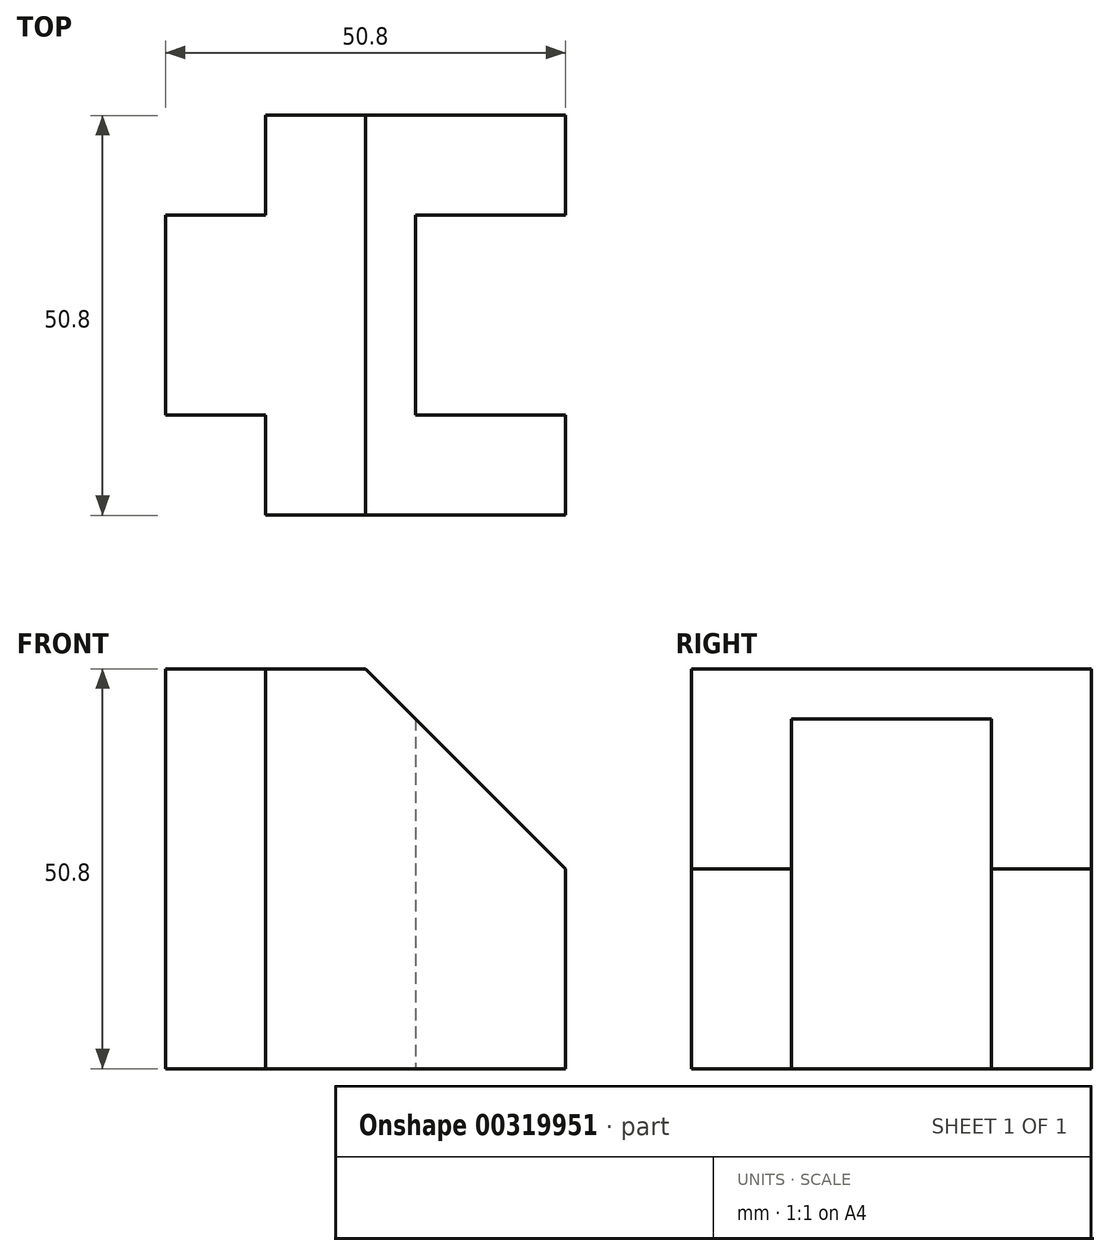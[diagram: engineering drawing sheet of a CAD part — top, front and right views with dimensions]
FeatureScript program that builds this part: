
annotation { "Feature Type Name" : "Feature", "Feature Type Description" : "" }
export const myFeature = defineFeature(function(context is Context, id is Id, definition is map)
    precondition{}
    {
        {
            var Q0;
            Q0=qCreatedBy(makeId("Top.planeOp"),FACE);
            var sketch = newSketch(context, id + "F0", { "sketchPlane" : qUnion([Q0])});
            skLineSegment(sketch, "E0", {"start": v(-18.83, 12.92) * mm, "end": v(6.57, 12.92) * mm});
            skLineSegment(sketch, "E1", {"start": v(6.57, 12.92) * mm, "end": v(19.27, 12.92) * mm});
            skLineSegment(sketch, "E2", {"start": v(19.27, 12.92) * mm, "end": v(19.27, 0.22) * mm});
            skLineSegment(sketch, "E3", {"start": v(19.27, 0.22) * mm, "end": v(0.22, 0.22) * mm});
            skLineSegment(sketch, "E4", {"start": v(0.22, 0.22) * mm, "end": v(0.22, -25.18) * mm});
            skLineSegment(sketch, "E5", {"start": v(0.22, -25.18) * mm, "end": v(19.27, -25.18) * mm});
            skLineSegment(sketch, "E6", {"start": v(19.27, -25.18) * mm, "end": v(19.27, -37.88) * mm});
            skLineSegment(sketch, "E7", {"start": v(19.27, -37.88) * mm, "end": v(6.57, -37.88) * mm});
            skLineSegment(sketch, "E8", {"start": v(6.57, -37.88) * mm, "end": v(-18.83, -37.88) * mm});
            skLineSegment(sketch, "E9", {"start": v(-18.83, -37.88) * mm, "end": v(-18.83, -25.18) * mm});
            skLineSegment(sketch, "E10", {"start": v(-18.83, -25.18) * mm, "end": v(-31.53, -25.18) * mm});
            skLineSegment(sketch, "E11", {"start": v(-31.53, -25.18) * mm, "end": v(-31.53, 0.22) * mm});
            skLineSegment(sketch, "E12", {"start": v(-31.53, 0.22) * mm, "end": v(-18.83, 0.22) * mm});
            skLineSegment(sketch, "E13", {"start": v(-18.83, 12.92) * mm, "end": v(-18.83, 0.22) * mm});
            skLineSegment(sketch, "E14", {"start": v(-6.13, 12.92) * mm, "end": v(-6.13, -37.88) * mm});
            skSolve(sketch);
        }
        {
            var Q0;
            Q0 = qSketchRegion(id + "F0", true);
            extrude(context, id + "F1", {"entities" : qUnion([Q0]), "depth" : 50.8 * mm});
        }
        {
            var Q0;
            Q0=makeQuery(id+"F1.opExtrude","SWEPT_FACE",FACE,{"disambiguationData":[OSD([sQuery(id+"F0.wireOp",EDGE,"E7"),sQuery(id+"F0.wireOp",EDGE,"E8")])]});
            var sketch = newSketch(context, id + "F2", { "sketchPlane" : qUnion([Q0])});
            skLineSegment(sketch, "E15", {"start": v(-6.13, 50.8) * mm, "end": v(19.27, 25.4) * mm});
            skLineSegment(sketch, "E16", {"start": v(19.27, 25.4) * mm, "end": v(19.27, 50.8) * mm});
            skLineSegment(sketch, "E17", {"start": v(19.27, 50.8) * mm, "end": v(-6.13, 50.8) * mm});
            skSolve(sketch);
        }
        {
            var Q0;
            Q0=makeQuery(id+"F2.imprint","IMPRINT",FACE,{"disambiguationData":[TD([[makeQuery(id+"F2.imprint","IMPRINT",EDGE,{"derivedFrom":sQuery(id+"F2.wireOp",EDGE,"E15")}),1.0]])]});
            extrude(context, id + "F3", {"entities" : qUnion([Q0]), "operationType" : NewBodyOperationType.REMOVE, "endBound" : BoundingType.THROUGH_ALL, "oppositeDirection" : true, "depth" : 25.4 * mm});
        }
    });
